# Revit family: FU_Inspec_Cajal_6-1
name_source: partatom
category: Furniture
units: mm (PartAtom-declared; Revit-internal decimal feet)

## family parameters
Always vertical = Yes
Cut with Voids When Loaded = No
OmniClass Number = 23.40.20.00
OmniClass Title = General Furniture and Specialties
Room Calculation Point = No
Shared = No
Work Plane-Based = No

## types (3) — shared parameters
Assembly Code = E2020
Depth = 57 mm  [stored 0.187008 ft]
Description = Easy chair with upholstered seat with plywood in molded high resilient polyurethane foam, on powder coated or chromium plated steel tubing.
Height = 77 mm  [stored 0.252625 ft]
Keynote = 46.B
Length = 62 mm  [stored 0.203412 ft]
Manufacturer = Inspec
Model = cajal 6.1
URL = https://inspecfurniture.com
Weight = 21 Kg
zero-valued in all types: Default Elevation

## per-type parameters (varying)
| type | Back Material | Frame Material | Seat Material |
| Leather | Leather - Rustical - Brown | Metal - Graphite - Glossy | Leather - Rustical - Brown |
| Fabric - Orange | Fabric - Orange | Metall - Eggshell - Glossy | Fabric - Orange |
| Fabric - Pastel Pink | Fabric - Pastel Pink | Metal - Chrome - Polished | Fabric - Pastel Pink |

note: [stored X ft] marks values corroborated as IEEE doubles in the binary element streams (Revit-internal decimal feet)

## geometry (parser evidence)
native form markers: Blend x12, Sweep x2
no freeform markers — native parametric forms only
